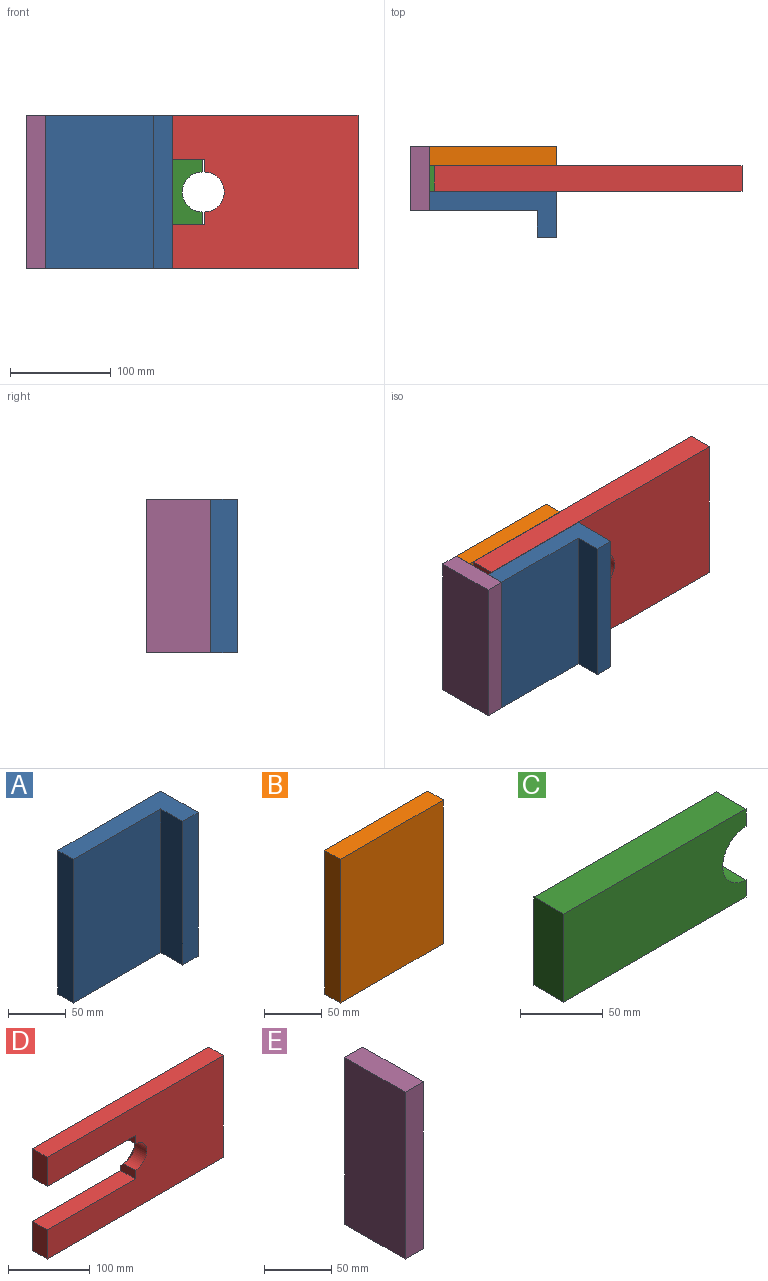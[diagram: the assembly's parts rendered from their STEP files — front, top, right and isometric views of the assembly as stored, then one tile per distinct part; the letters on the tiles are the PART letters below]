
ASSEMBLY  parts=5 mates=4
PART A: 8 faces, bbox 126.2x45.7x152.4 mm
  f0: plane 126.21x45.72mm, normal (0,0,1), area 2912.3mm2, adj f1,f2,f3,f4,f5,f6
  f1: plane 152.4x19.05mm, normal (-1,0,0), area 2903.2mm2, adj f0,f2,f6,f7
  f2: plane 152.4x126.21mm, normal (0,1,0), area 19233.8mm2, adj f0,f1,f3,f7
  f3: plane 152.4x45.72mm, normal (1,0,0), area 6967.7mm2, adj f0,f2,f4,f7
  f4: plane 152.4x19.05mm, normal (0,-1,0), area 2903.2mm2, adj f0,f3,f5,f7
  f5: plane 152.4x26.67mm, normal (-1,0,0), area 4064.5mm2, adj f0,f4,f6,f7
  f6: plane 152.4x107.16mm, normal (0,-1,0), area 16330.6mm2, adj f0,f1,f5,f7
  f7: plane 126.21x45.72mm, normal (0,0,-1), area 2912.3mm2, adj f1,f2,f3,f4,f5,f6
PART B: 6 faces, bbox 126.2x19.1x152.4 mm
  f0: plane 126.21x19.05mm, normal (0,0,1), area 2404.2mm2, adj f1,f2,f3,f4
  f1: plane 152.4x126.21mm, normal (0,1,0), area 19233.8mm2, adj f0,f2,f4,f5
  f2: plane 152.4x19.05mm, normal (1,0,0), area 2903.2mm2, adj f0,f1,f3,f5
  f3: plane 152.4x126.21mm, normal (0,-1,0), area 19233.8mm2, adj f0,f2,f4,f5
  f4: plane 152.4x19.05mm, normal (-1,0,0), area 2903.2mm2, adj f0,f1,f3,f5
  f5: plane 126.21x19.05mm, normal (0,0,-1), area 2404.2mm2, adj f1,f2,f3,f4
PART C: 9 faces, bbox 155.6x25.4x65.1 mm
  f0: plane 155.58x25.4mm, normal (0,0,-1), area 3951.6mm2, adj f1,f5,f6,f7
  f1: plane 25.4x12.7mm, normal (1,0,0), area 309.7mm2, adj f0,f2,f6,f7,f8
  f2: cylinder r=19.84mm len=39.69mm, axis (0,1,0), area 1266.8mm2, adj f1,f3,f6,f8
  f3: plane 25.4x12.7mm, normal (1,0,0), area 309.7mm2, adj f2,f4,f6,f7,f8
  f4: plane 155.58x25.4mm, normal (0,0,1), area 3951.6mm2, adj f3,f5,f6,f7
  f5: plane 65.09x25.4mm, normal (-1,0,0), area 1653.2mm2, adj f0,f4,f6,f7
  f6: plane 155.58x65.09mm, normal (0,-1,0), area 9507.4mm2, adj f0,f1,f2,f3,f4,f5
  f7: plane 155.58x65.09mm, normal (0,1,0), area 9150.2mm2, adj f0,f1,f3,f4,f5,f8
  f8: cone r=24.92mm half-angle=45deg, axis (0,1,0), area 505.2mm2, adj f1,f2,f3,f7
PART D: 13 faces, bbox 304.8x25.4x152.4 mm
  f0: plane 152.4x25.4mm, normal (0,0,-1), area 3871mm2, adj f1,f9,f10,f11
  f1: plane 25.4x12.7mm, normal (-1,0,0), area 309.7mm2, adj f0,f2,f10,f11,f12
  f2: cylinder r=19.84mm len=39.69mm, axis (0,1,0), area 1266.8mm2, adj f1,f3,f10,f12
  f3: plane 25.4x12.7mm, normal (-1,0,0), area 309.7mm2, adj f2,f4,f10,f11,f12
  f4: plane 152.4x25.4mm, normal (0,0,1), area 3871mm2, adj f3,f5,f10,f11
  f5: plane 43.66x25.4mm, normal (-1,0,0), area 1108.9mm2, adj f4,f6,f10,f11
  f6: plane 304.8x25.4mm, normal (0,0,-1), area 7741.9mm2, adj f5,f7,f10,f11
  f7: plane 152.4x25.4mm, normal (1,0,0), area 3871mm2, adj f6,f8,f10,f11
  f8: plane 304.8x25.4mm, normal (0,0,1), area 7741.9mm2, adj f7,f9,f10,f11
  f9: plane 43.66x25.4mm, normal (-1,0,0), area 1108.9mm2, adj f0,f8,f10,f11
  f10: plane 304.8x152.4mm, normal (0,-1,0), area 35913.6mm2, adj f0,f1,f2,f3,f4,f5,f6,f7
  f11: plane 304.8x152.4mm, normal (0,1,0), area 35556.4mm2, adj f0,f1,f3,f4,f5,f6,f7,f8
  f12: cone r=24.92mm half-angle=45deg, axis (0,1,0), area 505.2mm2, adj f1,f2,f3,f11
PART E: 6 faces, bbox 19.1x63.5x152.4 mm
  f0: plane 63.5x19.05mm, normal (0,0,1), area 1209.7mm2, adj f1,f3,f4,f5
  f1: plane 152.4x19.05mm, normal (0,-1,0), area 2903.2mm2, adj f0,f2,f3,f4
  f2: plane 63.5x19.05mm, normal (0,0,-1), area 1209.7mm2, adj f1,f3,f4,f5
  f3: plane 152.4x63.5mm, normal (1,0,0), area 9677.4mm2, adj f0,f1,f2,f5
  f4: plane 152.4x63.5mm, normal (-1,0,0), area 9677.4mm2, adj f0,f1,f2,f5
  f5: plane 152.4x19.05mm, normal (0,1,0), area 2903.2mm2, adj f0,f2,f3,f4
PLACE A t=(-1.81,0,0)mm
PLACE B t=(-1.81,0,0)mm
PLACE C t=(-1.81,0,0)mm
PLACE D at identity fixed
PLACE E t=(-1.81,0,0)mm
MATE fastened B.f4 <-> C.f5  axis (-1,0,0) through (-157.38,0,0)mm
MATE fastened A.f1 <-> C.f5  axis (-1,0,0) through (-157.38,-25.4,0)mm
MATE slider D.f5 <-> C.f5  axis (-1,0,0) through (-152.4,-25.4,-32.54)mm
MATE fastened B.f1 <-> E.f5  axis (0,1,0) through (-157.38,19.05,0)mm
